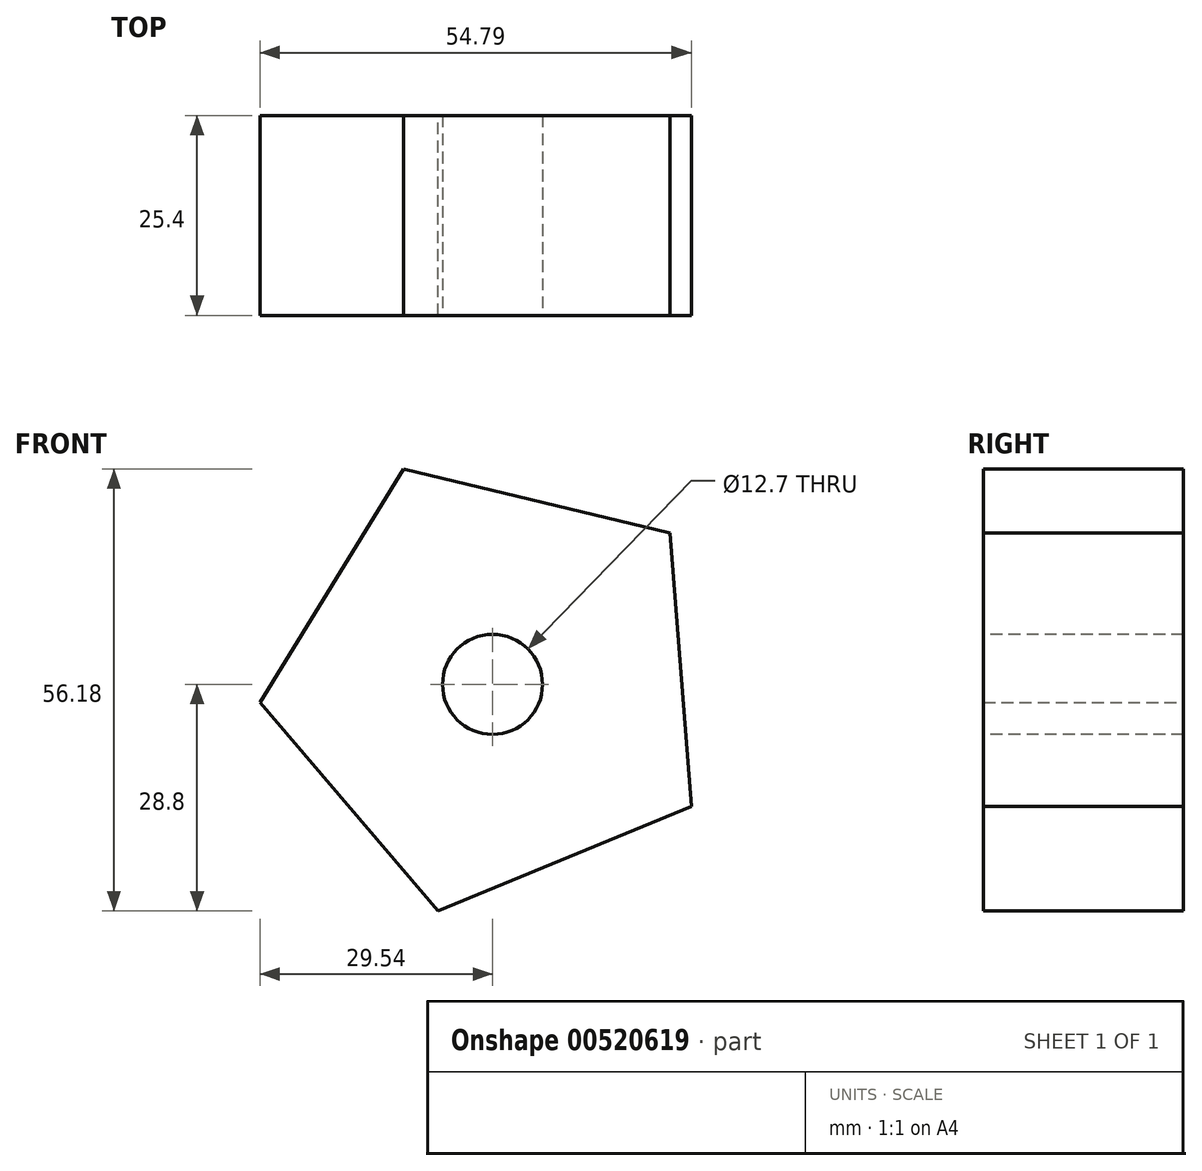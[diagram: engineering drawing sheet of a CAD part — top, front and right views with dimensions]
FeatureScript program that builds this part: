
annotation { "Feature Type Name" : "Feature", "Feature Type Description" : "" }
export const myFeature = defineFeature(function(context is Context, id is Id, definition is map)
    precondition{}
    {
        {
            var Q0;
            Q0=qCreatedBy(makeId("Front.planeOp"),FACE);
            var sketch = newSketch(context, id + "F0", { "sketchPlane" : qUnion([Q0])});
            skCircle(sketch, "E0.cCircle", {"center": v(0, 0) * mm, "radius": 23.97 * mm, "construction": true});
            skLineSegment(sketch, "E0.0", {"start": v(-29.54, -2.3) * mm, "end": v(-11.32, 27.38) * mm});
            skLineSegment(sketch, "E0.1", {"start": v(-11.32, 27.38) * mm, "end": v(22.54, 19.23) * mm});
            skLineSegment(sketch, "E0.2", {"start": v(22.54, 19.23) * mm, "end": v(25.25, -15.5) * mm});
            skLineSegment(sketch, "E0.3", {"start": v(25.25, -15.5) * mm, "end": v(-6.93, -28.8) * mm});
            skLineSegment(sketch, "E0.4", {"start": v(-6.93, -28.8) * mm, "end": v(-29.54, -2.3) * mm});
            skPoint(sketch, "E0.0.midPoint", {"position": v(-20.43, 12.54) * mm});
            skSolve(sketch);
        }
        {
            var Q0;
            Q0=makeQuery(id+"F0.imprint","IMPRINT",FACE,{"disambiguationData":[TD([[makeQuery(id+"F0.imprint","IMPRINT",EDGE,{"derivedFrom":sQuery(id+"F0.wireOp",EDGE,"E0.0")}),-1.0]])]});
            extrude(context, id + "F1", {"entities" : qUnion([Q0]), "depth" : 25.4 * mm, "offsetDistance" : 25.4 * mm});
        }
        {
            var Q0;
            Q0=makeQuery(id+"F1.opExtrude","CAP_FACE",FACE,{"disambiguationData":[OSD([sQuery(id+"F0.wireOp",EDGE,"E0.0"),sQuery(id+"F0.wireOp",EDGE,"E0.1"),sQuery(id+"F0.wireOp",EDGE,"E0.2"),sQuery(id+"F0.wireOp",EDGE,"E0.3"),sQuery(id+"F0.wireOp",EDGE,"E0.4")])],"isStart":false});
            var sketch = newSketch(context, id + "F2", { "sketchPlane" : qUnion([Q0])});
            skCircle(sketch, "E1", {"center": v(0, 0) * mm, "radius": 6.35 * mm});
            skSolve(sketch);
        }
        {
            var Q0;
            Q0=makeQuery(id+"F2.imprint","IMPRINT",FACE,{"disambiguationData":[TD([[makeQuery(id+"F2.imprint","IMPRINT",EDGE,{"derivedFrom":sQuery(id+"F2.wireOp",EDGE,"E1")}),1.0]])]});
            extrude(context, id + "F3", {"entities" : qUnion([Q0]), "operationType" : NewBodyOperationType.REMOVE, "oppositeDirection" : true, "depth" : 25.4 * mm, "offsetDistance" : 25.4 * mm});
        }
    });
